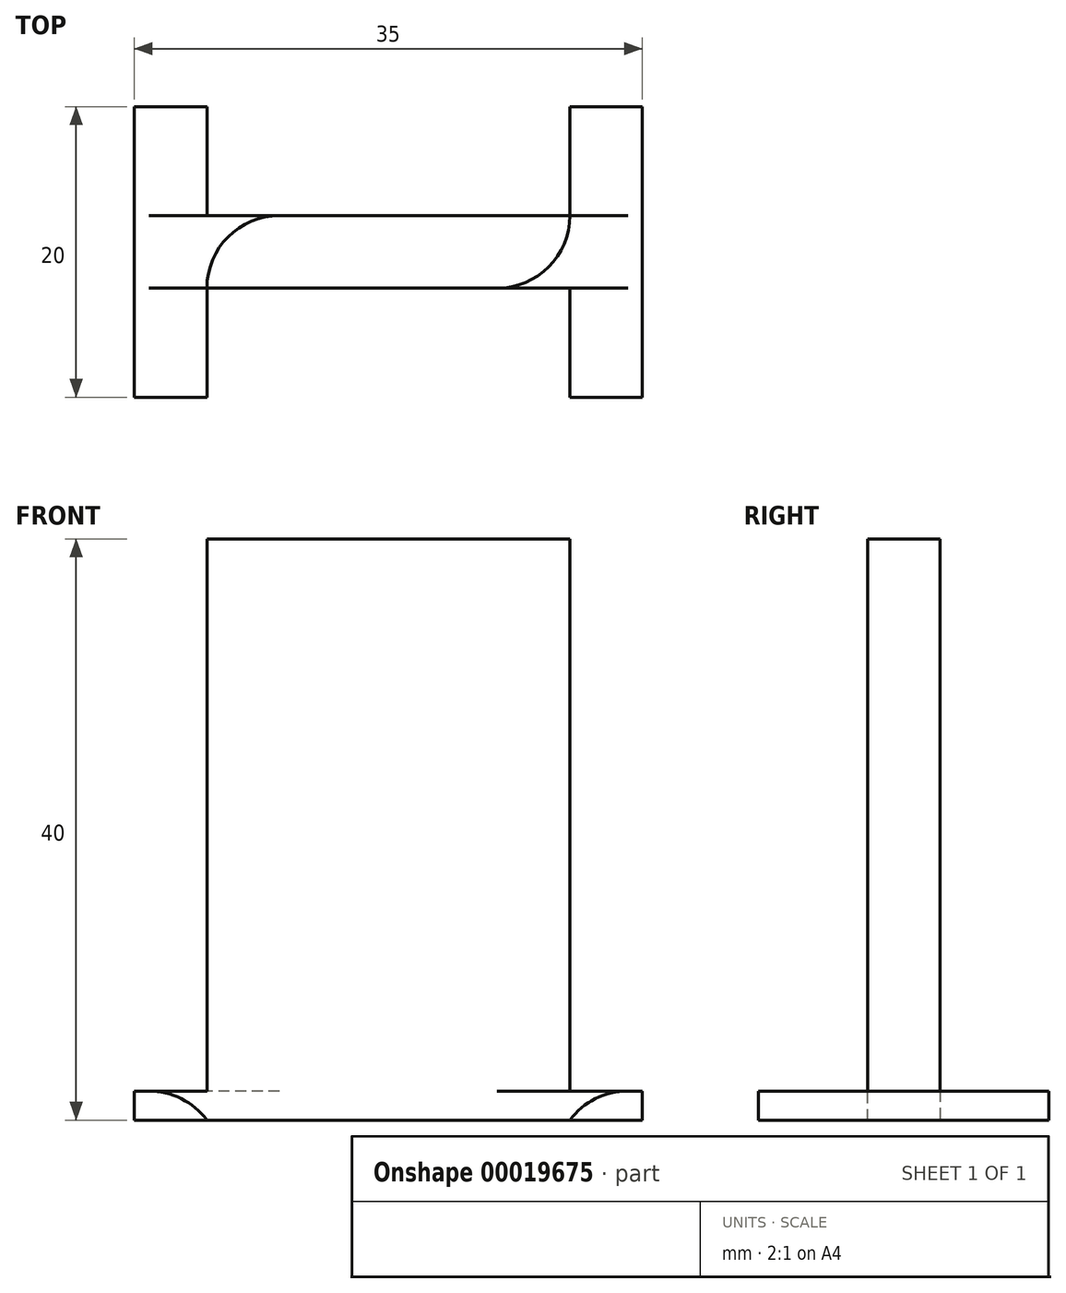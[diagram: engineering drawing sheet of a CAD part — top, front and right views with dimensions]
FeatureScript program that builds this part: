
annotation { "Feature Type Name" : "Feature", "Feature Type Description" : "" }
export const myFeature = defineFeature(function(context is Context, id is Id, definition is map)
    precondition{}
    {
        {
            var Q0;
            Q0=qCreatedBy(makeId("Top.planeOp"),FACE);
            var sketch = newSketch(context, id + "F0", { "sketchPlane" : qUnion([Q0])});
            skLineSegment(sketch, "E0.rect.bottom", {"start": v(12.5, -2.5) * mm, "end": v(-12.5, -2.5) * mm});
            skLineSegment(sketch, "E0.rect.top", {"start": v(12.5, 2.5) * mm, "end": v(-12.5, 2.5) * mm});
            skLineSegment(sketch, "E0.rect.left", {"start": v(12.5, -2.5) * mm, "end": v(12.5, 2.5) * mm});
            skLineSegment(sketch, "E0.rect.right", {"start": v(-12.5, -2.5) * mm, "end": v(-12.5, 2.5) * mm});
            skPoint(sketch, "E0.rect.middle", {"position": v(0, 0) * mm});
            skLineSegment(sketch, "E1", {"start": v(34.03, 0) * mm, "end": v(-32.39, 0) * mm, "construction": true});
            skLineSegment(sketch, "E2.rect.bottom", {"start": v(17.5, 10) * mm, "end": v(12.5, 10) * mm});
            skLineSegment(sketch, "E2.rect.top", {"start": v(17.5, -10) * mm, "end": v(12.5, -10) * mm});
            skLineSegment(sketch, "E2.rect.left", {"start": v(17.5, 10) * mm, "end": v(17.5, -10) * mm});
            skLineSegment(sketch, "E2.rect.right", {"start": v(12.5, 10) * mm, "end": v(12.5, -10) * mm});
            skPoint(sketch, "E2.rect.middle", {"position": v(15, 0) * mm});
            skLineSegment(sketch, "E3.rect.left", {"start": v(-12.5, 10) * mm, "end": v(-12.5, -10) * mm});
            skLineSegment(sketch, "E3.rect.bottom", {"start": v(-12.5, 10) * mm, "end": v(-17.5, 10) * mm});
            skLineSegment(sketch, "E3.rect.top", {"start": v(-12.5, -10) * mm, "end": v(-17.5, -10) * mm});
            skLineSegment(sketch, "E3.rect.right", {"start": v(-17.5, 10) * mm, "end": v(-17.5, -10) * mm});
            skSolve(sketch);
        }
        {
            var Q0;
            {var subQ2=sQuery(id+"F0.wireOp",EDGE,"E0.rect.bottom");Q0=makeQuery(id+"F0.imprint","IMPRINT",FACE,{"disambiguationData":[TD([[makeQuery(id+"F0.imprint","IMPRINT",EDGE,{"derivedFrom":subQ2}),-1.0]])]});}
            extrude(context, id + "F1", {"entities" : qUnion([Q0]), "depth" : 40 * mm});
        }
        {
            var Q0;
            {var subQ1=sQuery(id+"F0.wireOp",EDGE,"E3.rect.bottom");Q0=makeQuery(id+"F0.imprint","IMPRINT",FACE,{"disambiguationData":[TD([[makeQuery(id+"F0.imprint","IMPRINT",EDGE,{"derivedFrom":subQ1}),1.0]])]});}
            var Q1;
            {var subQ4=sQuery(id+"F0.wireOp",EDGE,"E2.rect.bottom");Q1=makeQuery(id+"F0.imprint","IMPRINT",FACE,{"disambiguationData":[TD([[makeQuery(id+"F0.imprint","IMPRINT",EDGE,{"derivedFrom":subQ4}),1.0]])]});}
            extrude(context, id + "F2", {"entities" : qUnion([Q0, Q1]), "operationType" : NewBodyOperationType.ADD, "depth" : 2 * mm});
        }
        {
            var Q0;
            {var subQ0=sQuery(id+"F0.wireOp",EDGE,"E2.rect.right");Q0=makeQuery(id+"F2.boolean.opBoolean","SPLIT",EDGE,{"disambiguationData":[topologyDisambiguationEdgeConnected([makeQuery(id+"F1.opExtrude","SWEPT_FACE",FACE,{"disambiguationData":[OSD([subQ0])]}),makeQuery(id+"F2.opExtrude","CAP_FACE",FACE,{"disambiguationData":[OSD([sQuery(id+"F0.wireOp",EDGE,"E2.rect.bottom"),sQuery(id+"F0.wireOp",EDGE,"E2.rect.top"),sQuery(id+"F0.wireOp",EDGE,"E2.rect.left"),subQ0])],"isStart":false})])],"derivedFrom":makeQuery(id+"F2.opExtrude","CAP_EDGE",EDGE,{"disambiguationData":[OSD([subQ0])],"isStart":false})});}
            var Q1;
            {var subQ0=sQuery(id+"F0.wireOp",EDGE,"E3.rect.left");Q1=makeQuery(id+"F2.boolean.opBoolean","SPLIT",EDGE,{"disambiguationData":[topologyDisambiguationEdgeConnected([makeQuery(id+"F1.opExtrude","SWEPT_FACE",FACE,{"disambiguationData":[OSD([subQ0])]}),makeQuery(id+"F2.opExtrude","CAP_FACE",FACE,{"disambiguationData":[OSD([subQ0,sQuery(id+"F0.wireOp",EDGE,"E3.rect.bottom"),sQuery(id+"F0.wireOp",EDGE,"E3.rect.top"),sQuery(id+"F0.wireOp",EDGE,"E3.rect.right")])],"isStart":false})])],"derivedFrom":makeQuery(id+"F2.opExtrude","CAP_EDGE",EDGE,{"disambiguationData":[OSD([subQ0])],"isStart":false})});}
            var Q2;
            Q2=makeQuery(id+"F1.opExtrude","CAP_EDGE",EDGE,{"disambiguationData":[OSD([sQuery(id+"F0.wireOp",EDGE,"E2.rect.right")])],"isStart":false});
            var Q3;
            Q3=makeQuery(id+"F1.opExtrude","CAP_EDGE",EDGE,{"disambiguationData":[OSD([sQuery(id+"F0.wireOp",EDGE,"E3.rect.left")])],"isStart":false});
            fillet(context, id + "F3", {"entities" : qUnion([Q0, Q1, Q2, Q3]), "radius" : 5 * mm, "allowEdgeOverflow" : false});
        }
        {
            var Q0;
            {var subQ0=sQuery(id+"F0.wireOp",EDGE,"E0.rect.top");var subQ1=sQuery(id+"F0.wireOp",EDGE,"E2.rect.right");Q0=makeQuery(id+"F2.boolean.opBoolean","SPLIT",EDGE,{"disambiguationData":[topologyDisambiguationEdgeConnected([makeQuery(id+"F2.opExtrude","SWEPT_FACE",FACE,{"disambiguationData":[OSD([subQ1])]})])],"derivedFrom":makeQuery(id+"F1.opExtrude","SWEPT_EDGE",EDGE,{"disambiguationData":[OSD([subQ0,subQ1])]})});}
            var Q1;
            {var subQ0=sQuery(id+"F0.wireOp",EDGE,"E0.rect.top");var subQ1=sQuery(id+"F0.wireOp",EDGE,"E3.rect.left");Q1=makeQuery(id+"F2.boolean.opBoolean","SPLIT",EDGE,{"disambiguationData":[topologyDisambiguationEdgeConnected([makeQuery(id+"F2.opExtrude","SWEPT_FACE",FACE,{"disambiguationData":[OSD([subQ1])]})])],"derivedFrom":makeQuery(id+"F1.opExtrude","SWEPT_EDGE",EDGE,{"disambiguationData":[OSD([subQ0,subQ1])]})});}
            var Q2;
            {var subQ0=sQuery(id+"F0.wireOp",EDGE,"E0.rect.bottom");var subQ1=sQuery(id+"F0.wireOp",EDGE,"E2.rect.right");Q2=makeQuery(id+"F2.boolean.opBoolean","SPLIT",EDGE,{"disambiguationData":[topologyDisambiguationEdgeConnected([makeQuery(id+"F2.opExtrude","SWEPT_FACE",FACE,{"disambiguationData":[OSD([subQ1])]})])],"derivedFrom":makeQuery(id+"F1.opExtrude","SWEPT_EDGE",EDGE,{"disambiguationData":[OSD([subQ0,subQ1])]})});}
            var Q3;
            {var subQ0=sQuery(id+"F0.wireOp",EDGE,"E0.rect.bottom");var subQ1=sQuery(id+"F0.wireOp",EDGE,"E3.rect.left");Q3=makeQuery(id+"F2.boolean.opBoolean","SPLIT",EDGE,{"disambiguationData":[topologyDisambiguationEdgeConnected([makeQuery(id+"F2.opExtrude","SWEPT_FACE",FACE,{"disambiguationData":[OSD([subQ1])]})])],"derivedFrom":makeQuery(id+"F1.opExtrude","SWEPT_EDGE",EDGE,{"disambiguationData":[OSD([subQ0,subQ1])]})});}
            fillet(context, id + "F4", {"entities" : qUnion([Q0, Q1, Q2, Q3]), "radius" : 5 * mm, "tangentPropagation" : true, "allowEdgeOverflow" : false});
        }
    });
